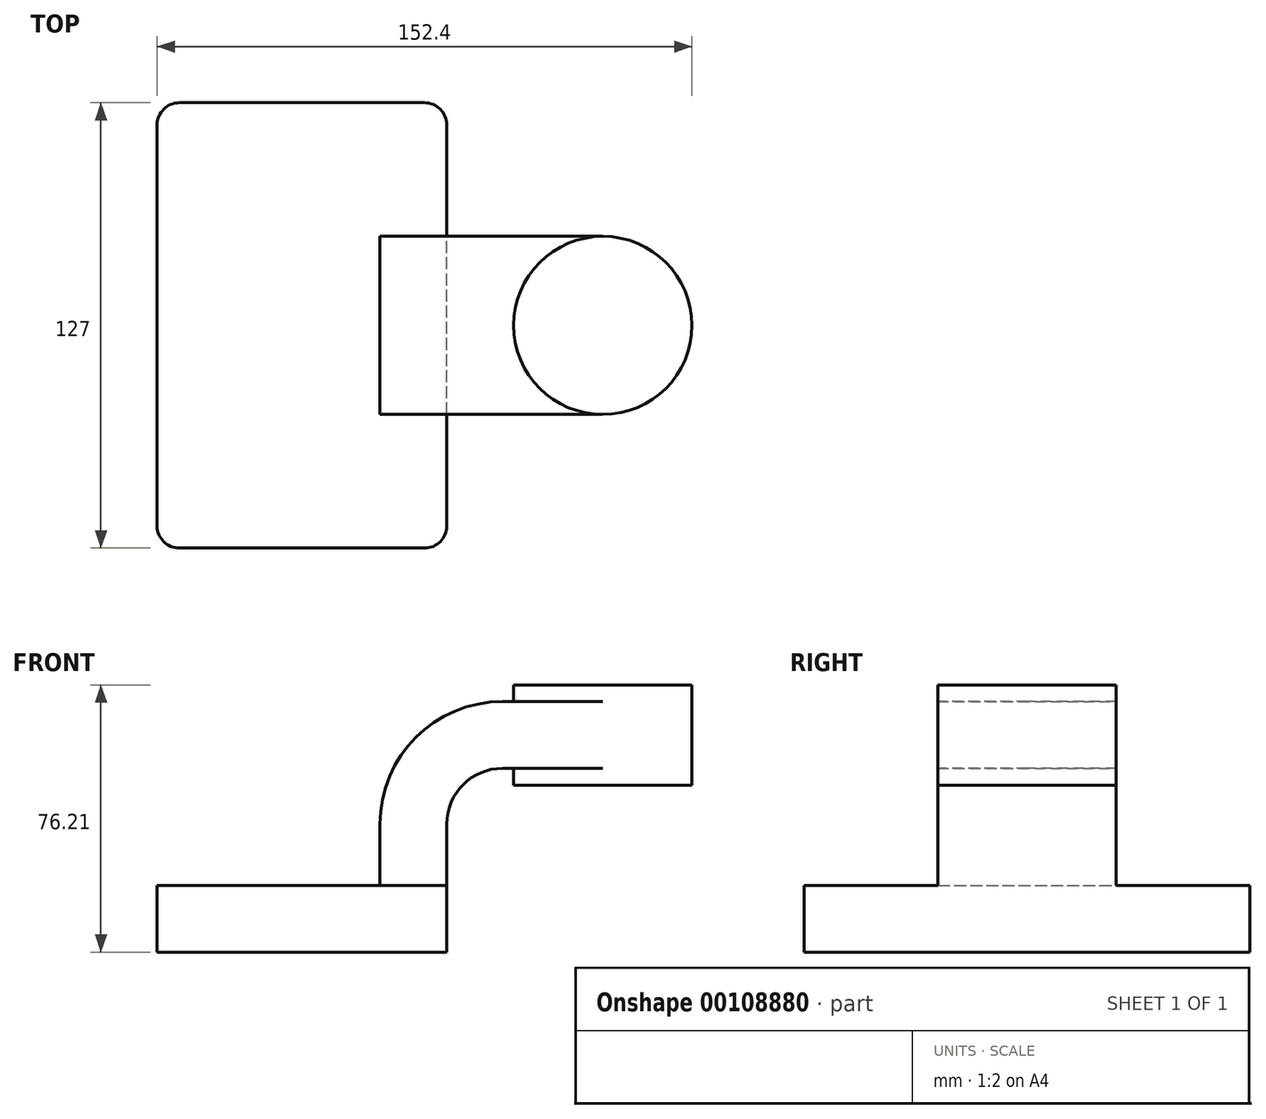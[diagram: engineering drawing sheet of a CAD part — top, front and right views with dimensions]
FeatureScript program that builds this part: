
annotation { "Feature Type Name" : "Feature", "Feature Type Description" : "" }
export const myFeature = defineFeature(function(context is Context, id is Id, definition is map)
    precondition{}
    {
        {
            var Q0;
            Q0=qCreatedBy(makeId("Front.planeOp"),FACE);
            var sketch = newSketch(context, id + "F0", { "sketchPlane" : qUnion([Q0])});
            skLineSegment(sketch, "E0.bottom", {"start": v(-41.28, -9.53) * mm, "end": v(41.28, -9.53) * mm});
            skLineSegment(sketch, "E0.top", {"start": v(-41.28, 9.52) * mm, "end": v(41.28, 9.52) * mm});
            skLineSegment(sketch, "E0.left", {"start": v(-41.28, -9.53) * mm, "end": v(-41.28, 9.52) * mm});
            skLineSegment(sketch, "E0.right", {"start": v(41.28, -9.53) * mm, "end": v(41.28, 9.52) * mm});
            skPoint(sketch, "E0.middle", {"position": v(0, 0) * mm});
            skLineSegment(sketch, "E1.bottom", {"start": v(60.32, 38.1) * mm, "end": v(111.12, 38.1) * mm});
            skLineSegment(sketch, "E1.top", {"start": v(60.32, 66.67) * mm, "end": v(111.12, 66.67) * mm});
            skLineSegment(sketch, "E1.left", {"start": v(60.32, 38.1) * mm, "end": v(60.32, 66.67) * mm});
            skLineSegment(sketch, "E1.right", {"start": v(111.12, 38.1) * mm, "end": v(111.12, 66.67) * mm});
            skPoint(sketch, "E1.middle", {"position": v(85.72, 52.39) * mm});
            skLineSegment(sketch, "E2", {"start": v(41.27, 9.52) * mm, "end": v(41.27, 27) * mm});
            skArc(sketch, "E3", {"start": v(41.27, 27) * mm, "mid": v(45.92, 38.23) * mm, "end": v(57.15, 42.88) * mm});
            skLineSegment(sketch, "E4", {"start": v(57.15, 42.88) * mm, "end": v(85.72, 42.88) * mm});
            skLineSegment(sketch, "E5.0", {"start": v(57.15, 61.93) * mm, "end": v(85.72, 61.93) * mm});
            skArc(sketch, "E5.1", {"start": v(22.22, 27) * mm, "mid": v(32.45, 51.7) * mm, "end": v(57.15, 61.93) * mm});
            skLineSegment(sketch, "E5.2", {"start": v(22.23, 9.52) * mm, "end": v(22.23, 27) * mm});
            skLineSegment(sketch, "E6", {"start": v(85.72, 38.1) * mm, "end": v(85.72, 66.67) * mm});
            skFitSpline(sketch, "E7", {"points": [v(-41.28, 9.53) * mm, v(57.15, 61.93) * mm], "startDerivative": vector(106.6, 153.69) * mm, "endDerivative": vector(74.69, -69.4) * mm});
            skSolve(sketch);
        }
        {
            var Q0;
            Q0=makeQuery(id+"F0.imprint","IMPRINT",FACE,{"disambiguationData":[TD([[makeQuery(id+"F0.imprint","IMPRINT",EDGE,{"derivedFrom":sQuery(id+"F0.wireOp",EDGE,"E0.bottom")}),1.0]])]});
            extrude(context, id + "F1", {"entities" : qUnion([Q0]), "endBound" : BoundingType.SYMMETRIC, "depth" : 127 * mm});
        }
        {
            var Q0;
            {var subQ1=sQuery(id+"F0.wireOp",EDGE,"E2");Q0=makeQuery(id+"F0.imprint","IMPRINT",FACE,{"disambiguationData":[TD([[makeQuery(id+"F0.imprint","IMPRINT",EDGE,{"derivedFrom":subQ1}),1.0]])]});}
            var Q1;
            {var subQ0=sQuery(id+"F0.wireOp",EDGE,"E4");var subQ1=sQuery(id+"F0.wireOp",EDGE,"E1.left");var subQ2=makeQuery(id+"F0.imprint","INTERSECT",VERTEX,{"derivedFrom":[subQ1,subQ0]});Q1=makeQuery(id+"F0.imprint","IMPRINT",FACE,{"disambiguationData":[TD([[makeQuery(id+"F0.imprint","IMPRINT",EDGE,{"disambiguationData":[TD([[subQ2,-1.0]])],"derivedFrom":subQ1}),-1.0]])]});}
            extrude(context, id + "F2", {"entities" : qUnion([Q0, Q1]), "operationType" : NewBodyOperationType.ADD, "endBound" : BoundingType.SYMMETRIC, "depth" : 50.8 * mm});
        }
        {
            var Q0;
            Q0=makeQuery(id+"F0.imprint","IMPRINT",FACE,{"disambiguationData":[TD([[makeQuery(id+"F0.imprint","IMPRINT",EDGE,{"derivedFrom":sQuery(id+"F0.wireOp",EDGE,"E5.1")}),1.0]])]});
            extrude(context, id + "F3", {"entities" : qUnion([Q0]), "operationType" : NewBodyOperationType.ADD, "endBound" : BoundingType.SYMMETRIC, "depth" : 15.88 * mm});
        }
        {
            var Q0;
            {var subQ0=sQuery(id+"F0.wireOp",EDGE,"E1.right");Q0=makeQuery(id+"F0.imprint","IMPRINT",FACE,{"disambiguationData":[TD([[makeQuery(id+"F0.imprint","IMPRINT",EDGE,{"derivedFrom":subQ0}),1.0]])]});}
            var Q1;
            Q1=sQuery(id+"F0.wireOp",EDGE,"E6");
            revolve(context, id + "F4", {"operationType" : NewBodyOperationType.ADD, "entities" : qUnion([Q0]), "axis" : qUnion([Q1]), "revolveType" : RevolveType.FULL});
        }
        {
            var Q0;
            Q0=makeQuery(id+"F1.opExtrude","CAP_EDGE",EDGE,{"disambiguationData":[OSD([sQuery(id+"F0.wireOp",EDGE,"E0.right")])],"isStart":false});
            var Q1;
            Q1=makeQuery(id+"F1.opExtrude","CAP_EDGE",EDGE,{"disambiguationData":[OSD([sQuery(id+"F0.wireOp",EDGE,"E0.left")])],"isStart":false});
            var Q2;
            Q2=makeQuery(id+"F1.opExtrude","CAP_EDGE",EDGE,{"disambiguationData":[OSD([sQuery(id+"F0.wireOp",EDGE,"E0.right")])],"isStart":true});
            var Q3;
            Q3=makeQuery(id+"F1.opExtrude","CAP_EDGE",EDGE,{"disambiguationData":[OSD([sQuery(id+"F0.wireOp",EDGE,"E0.left")])],"isStart":true});
            fillet(context, id + "F5", {"entities" : qUnion([Q0, Q1, Q2, Q3]), "radius" : 6.35 * mm, "tangentPropagation" : true, "allowEdgeOverflow" : false});
        }
    });
